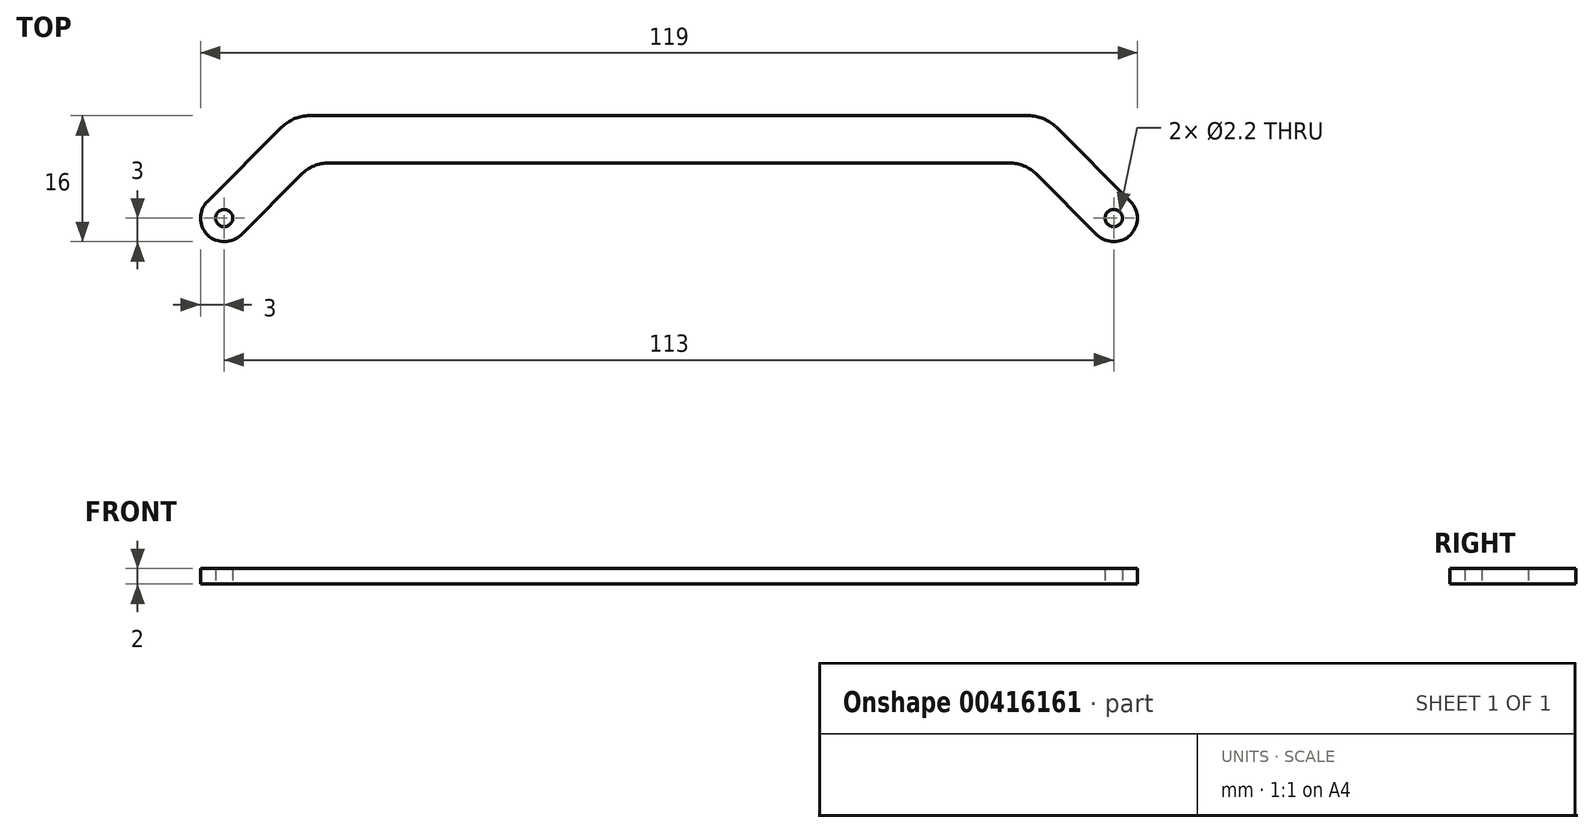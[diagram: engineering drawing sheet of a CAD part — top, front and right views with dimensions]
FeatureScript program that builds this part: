
annotation { "Feature Type Name" : "Feature", "Feature Type Description" : "" }
export const myFeature = defineFeature(function(context is Context, id is Id, definition is map)
    precondition{}
    {
        {
            var Q0;
            Q0=qCreatedBy(makeId("Top.planeOp"),FACE);
            var sketch = newSketch(context, id + "F0", { "sketchPlane" : qUnion([Q0])});
            skCircle(sketch, "E0", {"center": v(56.5, 0) * mm, "radius": 3 * mm});
            skLineSegment(sketch, "E1", {"start": v(58.62, 2.12) * mm, "end": v(49.2, 11.54) * mm});
            skLineSegment(sketch, "E2", {"start": v(45.67, 13) * mm, "end": v(0, 13) * mm});
            skLineSegment(sketch, "E3", {"start": v(0, 13) * mm, "end": v(0, 7) * mm});
            skLineSegment(sketch, "E4", {"start": v(0, 7) * mm, "end": v(43.19, 7) * mm});
            skLineSegment(sketch, "E5", {"start": v(46.72, 5.54) * mm, "end": v(54.38, -2.12) * mm});
            skLineSegment(sketch, "E6", {"start": v(37.07, 23.68) * mm, "end": v(32.82, 19.43) * mm, "construction": true});
            skPoint(sketch, "E7.visualSharp", {"position": v(45.26, 7) * mm});
            skArc(sketch, "E7.filletArc", {"start": v(46.72, 5.54) * mm, "mid": v(45.1, 6.62) * mm, "end": v(43.19, 7) * mm});
            skPoint(sketch, "E8.visualSharp", {"position": v(47.74, 13) * mm});
            skArc(sketch, "E8.filletArc", {"start": v(49.2, 11.54) * mm, "mid": v(47.58, 12.62) * mm, "end": v(45.67, 13) * mm});
            skCircle(sketch, "E9", {"center": v(56.5, 0) * mm, "radius": 1.1 * mm});
            skSolve(sketch);
        }
        {
            var Q0;
            Q0 = qSketchRegion(id + "F0", true);
            extrude(context, id + "F1", {"entities" : qUnion([Q0]), "depth" : 2 * mm, "offsetDistance" : 25 * mm});
        }
        {
            var Q0;
            Q0=makeQuery(id+"F1.opExtrude","SWEPT_BODY",BODY,{"disambiguationData":[OSD([sQuery(id+"F0.wireOp",EDGE,"E0"),sQuery(id+"F0.wireOp",EDGE,"E1"),sQuery(id+"F0.wireOp",EDGE,"E2"),sQuery(id+"F0.wireOp",EDGE,"E3"),sQuery(id+"F0.wireOp",EDGE,"E4"),sQuery(id+"F0.wireOp",EDGE,"E5"),sQuery(id+"F0.wireOp",EDGE,"E7.filletArc"),sQuery(id+"F0.wireOp",EDGE,"E8.filletArc"),sQuery(id+"F0.wireOp",EDGE,"E9")])]});
            var Q1;
            Q1=makeQuery(id+"F1.opExtrude","SWEPT_FACE",FACE,{"disambiguationData":[OSD([sQuery(id+"F0.wireOp",EDGE,"E3")])]});
            mirror(context, id + "F2", {"operationType" : NewBodyOperationType.ADD, "entities" : qUnion([Q0]), "mirrorPlane" : qUnion([Q1])});
        }
    });
